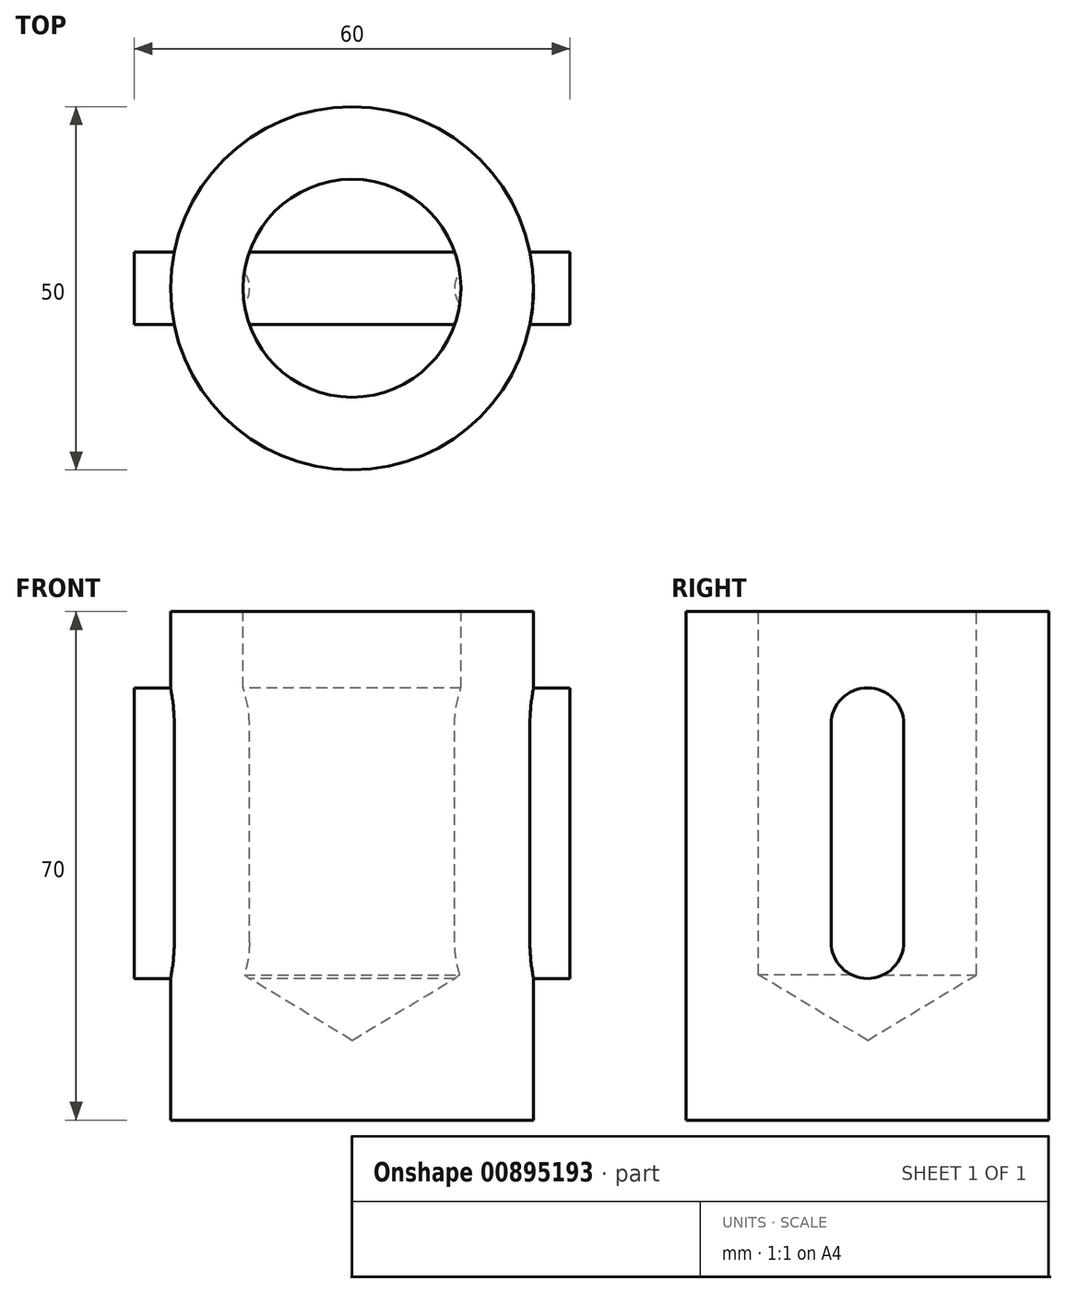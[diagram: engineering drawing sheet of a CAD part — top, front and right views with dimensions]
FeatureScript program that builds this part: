
annotation { "Feature Type Name" : "Feature", "Feature Type Description" : "" }
export const myFeature = defineFeature(function(context is Context, id is Id, definition is map)
    precondition{}
    {
        {
            var Q0;
            Q0=qCreatedBy(makeId("Top.planeOp"),FACE);
            var sketch = newSketch(context, id + "F0", { "sketchPlane" : qUnion([Q0])});
            skCircle(sketch, "E0", {"center": v(0, 0) * mm, "radius": 25 * mm});
            skSolve(sketch);
        }
        {
            var Q0;
            Q0=makeQuery(id+"F0.imprint","IMPRINT",FACE,{"disambiguationData":[TD([[makeQuery(id+"F0.imprint","IMPRINT",EDGE,{"derivedFrom":sQuery(id+"F0.wireOp",EDGE,"E0")}),1.0]])]});
            extrude(context, id + "F1", {"entities" : qUnion([Q0]), "depth" : 70 * mm, "offsetDistance" : 25 * mm});
        }
        {
            var Q0;
            Q0=makeQuery(id+"F1.opExtrude","CAP_FACE",FACE,{"disambiguationData":[OSD([sQuery(id+"F0.wireOp",EDGE,"E0")])],"isStart":false});
            var sketch = newSketch(context, id + "F2", { "sketchPlane" : qUnion([Q0])});
            skCircle(sketch, "E1", {"center": v(0, 0) * mm, "radius": 15 * mm});
            skSolve(sketch);
        }
        {
            var Q0;
            Q0=sQuery(id+"F2.wireOp",VERTEX,"E1.center");
            var Q1;
            Q1=makeQuery(id+"F1.opExtrude","SWEPT_BODY",BODY,{"disambiguationData":[OSD([sQuery(id+"F0.wireOp",EDGE,"E0")])]});
            hole(context, id + "F3", {"style" : HoleStyle.SIMPLE, "endStyle" : HoleEndStyle.BLIND, "holeDiameter" : 30 * mm, "majorDiameter" : 5 * mm, "holeDepth" : 50 * mm, "isTappedThrough" : true, "tappedDepth" : 12 * mm, "tapClearance" : 3, "locations" : qUnion([Q0]), "scope" : qUnion([Q1])});
        }
        {
            var Q0;
            Q0=qCreatedBy(makeId("Right.planeOp"),FACE);
            var sketch = newSketch(context, id + "F4", { "sketchPlane" : qUnion([Q0])});
            skLineSegment(sketch, "E2.bottom", {"start": v(-5, 54.5) * mm, "end": v(5, 54.5) * mm});
            skLineSegment(sketch, "E2.top", {"start": v(-5, 24.5) * mm, "end": v(5, 24.5) * mm});
            skLineSegment(sketch, "E2.left", {"start": v(-5, 54.5) * mm, "end": v(-5, 24.5) * mm});
            skLineSegment(sketch, "E2.right", {"start": v(5, 54.5) * mm, "end": v(5, 24.5) * mm});
            skArc(sketch, "E3", {"start": v(5, 54.5) * mm, "mid": v(0, 59.5) * mm, "end": v(-5, 54.5) * mm});
            skArc(sketch, "E4", {"start": v(-5, 24.5) * mm, "mid": v(0, 19.5) * mm, "end": v(5, 24.5) * mm});
            skSolve(sketch);
        }
        {
            var Q0;
            Q0 = qSketchRegion(id + "F4", true);
            extrude(context, id + "F5", {"entities" : qUnion([Q0]), "operationType" : NewBodyOperationType.ADD, "endBound" : BoundingType.SYMMETRIC, "depth" : 60 * mm, "offsetDistance" : 25 * mm});
        }
    });
